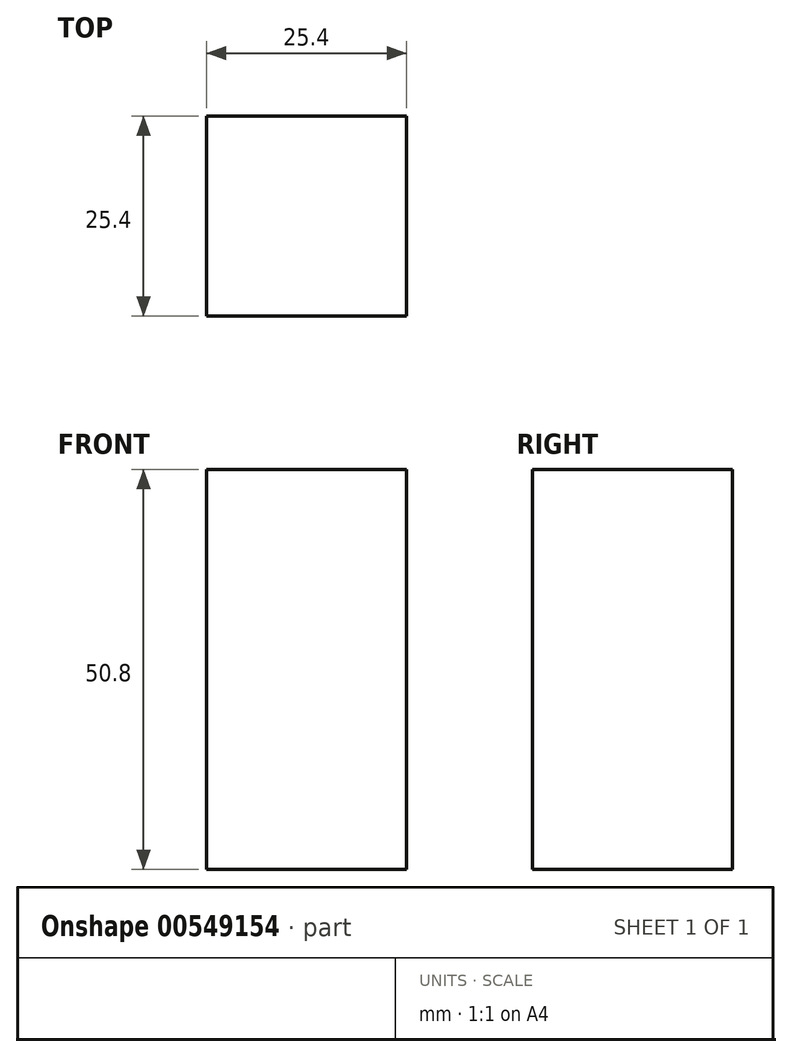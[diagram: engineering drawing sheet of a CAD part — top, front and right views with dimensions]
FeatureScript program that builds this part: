
annotation { "Feature Type Name" : "Feature", "Feature Type Description" : "" }
export const myFeature = defineFeature(function(context is Context, id is Id, definition is map)
    precondition{}
    {
        {
            var Q0;
            Q0=qCreatedBy(makeId("Front.planeOp"),FACE);
            var sketch = newSketch(context, id + "F0", { "sketchPlane" : qUnion([Q0])});
            skLineSegment(sketch, "E0", {"start": v(0, 0) * mm, "end": v(0, 50.8) * mm});
            skLineSegment(sketch, "E1", {"start": v(0, 50.8) * mm, "end": v(25.4, 50.8) * mm});
            skLineSegment(sketch, "E2", {"start": v(25.4, 50.8) * mm, "end": v(25.4, 0) * mm});
            skLineSegment(sketch, "E3", {"start": v(25.4, 0) * mm, "end": v(0, 0) * mm});
            skSolve(sketch);
        }
        {
            var Q0;
            Q0=makeQuery(id+"F0.imprint","IMPRINT",FACE,{"disambiguationData":[TD([[makeQuery(id+"F0.imprint","IMPRINT",EDGE,{"derivedFrom":sQuery(id+"F0.wireOp",EDGE,"E0")}),-1.0]])]});
            extrude(context, id + "F1", {"entities" : qUnion([Q0]), "depth" : 25.4 * mm});
        }
    });
